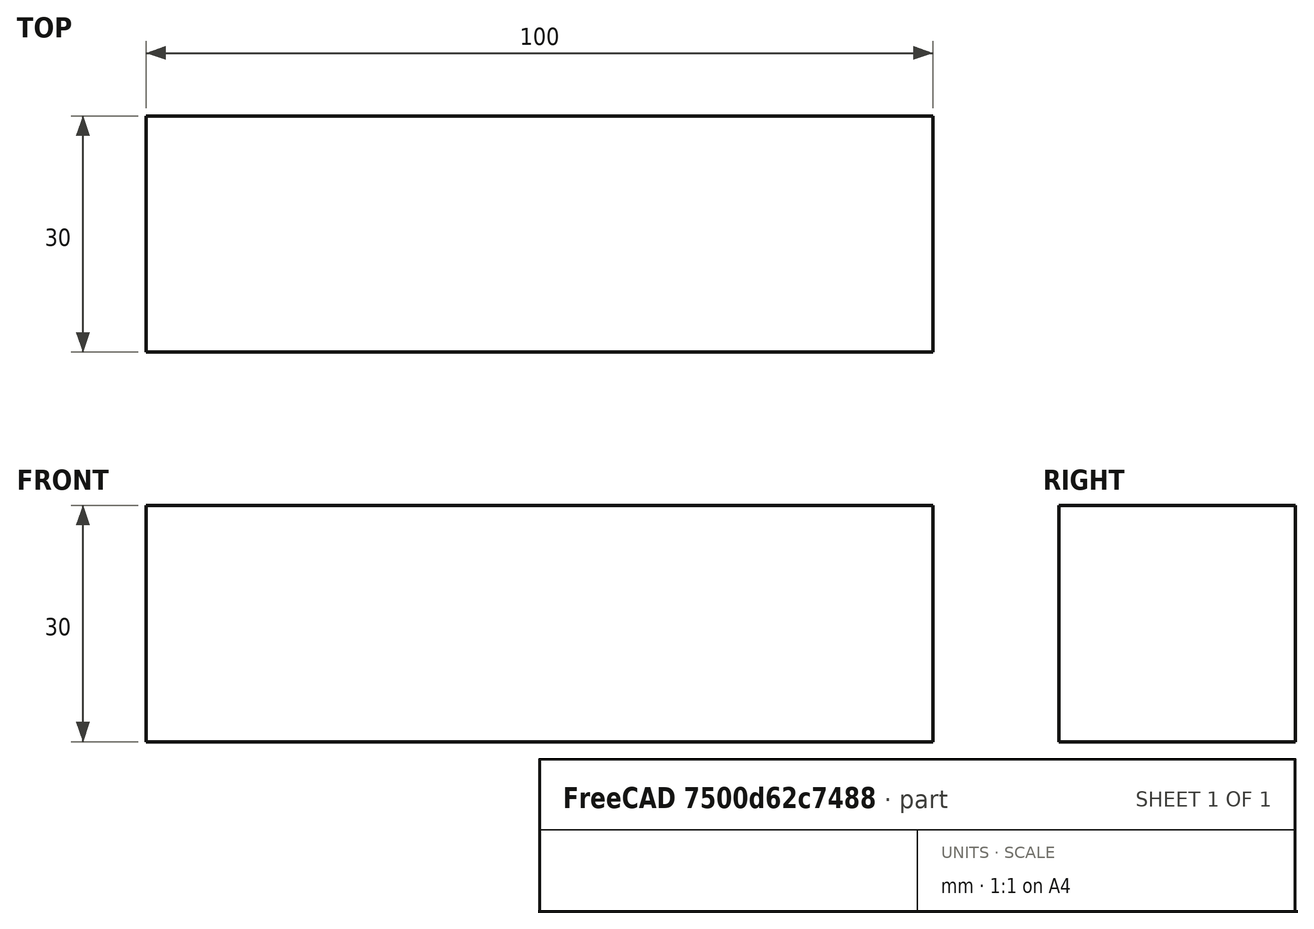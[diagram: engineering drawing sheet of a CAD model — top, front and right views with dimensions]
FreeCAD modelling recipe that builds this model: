
FCSTD DOCUMENT  (FreeCAD 0.19R)
Label: TestCfd
License: All rights reserved
LicenseURL: http://en.wikipedia.org/wiki/All_rights_reserved
objects: Fem::ConstraintFluidBoundary×3, Part::Box×1, Fem::FemSolverObjectPython×1, App::MaterialObjectPython×1, Fem::FemMeshObjectPython×1, Fem::FemAnalysisPython×1
note: 1 computed .brp shape members not serialized (recipe doc carries the construction recipe); baked Part::Feature solids carry a one-line shape summary decoded from their .brp

FEATURE [Part::Box] Box  label="Cube"
  AttacherType = Attacher::AttachEngine3D
  Height = 30
  Length = 100
  Width = 30
FEATURE [Fem::FemSolverObjectPython] OpenFOAM  # FEM object (typed FeaturePython)
  Buoyant = false
  Compressible = false
  DynamicMeshing = false
  EndTime = 0
  Gravity = (0,0,0)
  HeatTransfering = false
  InputCaseName = TestCase
  NonNewtonian = false
  Parallel = false
  PhysicalDomain = 1
  Porous = false
  PotentialInit = false
  ResultObtained = true
  SolverName = OpenFOAM
  StartTime = 0
  TimeStep = 0
  Transient = false
  Transonic = false
  Turbulence = 1
  TurbulenceModel = 8
  WriteInterval = 0
FEATURE [App::MaterialObjectPython] FluidMaterial  # material (typed FeaturePython)
  Category = 1
  Material = CardName=Water,Density=998 kg/m^3,Description=Standard distilled water properties at 20 Degrees Celsius and 1 atm,DynamicViscosity=1.003e-3 kg/m/s,+7 more (map truncated)
FEATURE [Fem::FemMeshObjectPython] Box_Mesh  # FEM object (typed FeaturePython)
  Algorithm2D = 0
  Algorithm3D = 0
  CharacteristicLengthMax = 2
  CharacteristicLengthMin = 0
  CoherenceMesh = true
  ElementDimension = 0
  ElementOrder = 0
  GeometryTolerance = 1e-06
  HighOrderOptimize = false
  LengthScalingFactor = 1
  OptimizeNetgen = false
  OptimizeStd = false
  OutputFormat = 1
  Part = -> Box
  RecombineAll = false
FEATURE [Fem::ConstraintFluidBoundary] ConstraintFluidBoundary
  BoundaryType = 1
  BoundaryValue = 0
  DirectionVector = (0,1,0)
  HTCoeffValue = 0
  HeatFluxValue = 0
  NormalDirection = (0,1,0)
  Normals = (64) [(0,1,0),(0,1,0),(0,1,0),(0,1,0),(0,1,0),(0,1,0),(0,1,0),(0,1,0),(0,1,0),(0,1,0),(0,1,0),(0,1,0),(0,1,0),(0,1,0),(0,1,0),(0,1,0),(0,0,1),(0,0,1),+46 more]
  Points = (64) [(0,30,0),(0,30,10),(0,30,20),(0,30,30),(33.3333,30,0),(33.3333,30,10),(33.3333,30,20),(33.3333,30,30),(66.6667,30,0),(66.6667,30,10),(66.6667,30,20),+53 more]
  References = -> [Box]
  Scale = 7
  Subtype = 1
  TemperatureValue = 0
  ThermalBoundaryType = 1
  TurbulenceSpecification = 1
  TurbulentIntensityValue = 0
  TurbulentLengthValue = 0
FEATURE [Fem::ConstraintFluidBoundary] ConstraintFluidBoundary001
  BoundaryType = 0
  BoundaryValue = 1
  DirectionVector = (1,0,0)
  HTCoeffValue = 0
  HeatFluxValue = 0
  NormalDirection = (-1,0,0)
  Normals = (16) [(-1,0,0),(-1,0,0),(-1,0,0),(-1,0,0),(-1,0,0),(-1,0,0),(-1,0,0),(-1,0,0),(-1,0,0),(-1,0,0),(-1,0,0),(-1,0,0),(-1,0,0),(-1,0,0),(-1,0,0),(-1,0,0)]
  Points = (16) [(0,30,0),(0,30,10),(0,30,20),(0,30,30),(0,20,0),(0,20,10),(0,20,20),(0,20,30),(0,10,0),(0,10,10),(0,10,20),(0,10,30),(0,0,0),(0,0,10),(0,0,20),+1 more]
  References = -> [Box]
  Reversed = true
  Scale = 4
  Subtype = 2
  TemperatureValue = 0
  ThermalBoundaryType = 1
  TurbulenceSpecification = 1
  TurbulentIntensityValue = 0
  TurbulentLengthValue = 0
FEATURE [Fem::ConstraintFluidBoundary] ConstraintFluidBoundary002
  BoundaryType = 2
  BoundaryValue = 10000
  DirectionVector = (1,0,0)
  HTCoeffValue = 0
  HeatFluxValue = 0
  NormalDirection = (1,0,0)
  Normals = (16) [(1,0,0),(1,0,0),(1,0,0),(1,0,0),(1,0,0),(1,0,0),(1,0,0),(1,0,0),(1,0,0),(1,0,0),(1,0,0),(1,0,0),(1,0,0),(1,0,0),(1,0,0),(1,0,0)]
  Points = (16) [(100,30,0),(100,30,10),(100,30,20),(100,30,30),(100,20,0),(100,20,10),(100,20,20),(100,20,30),(100,10,0),(100,10,10),(100,10,20),(100,10,30),+4 more]
  References = -> [Box]
  Scale = 4
  Subtype = 1
  TemperatureValue = 0
  ThermalBoundaryType = 1
  TurbulenceSpecification = 1
  TurbulentIntensityValue = 0
  TurbulentLengthValue = 0
FEATURE [Fem::FemAnalysisPython] CfdAnalysis  # FEM object (typed FeaturePython)
  Group = -> [OpenFOAM,FluidMaterial,Box_Mesh,ConstraintFluidBoundary,ConstraintFluidBoundary001,ConstraintFluidBoundary002]
